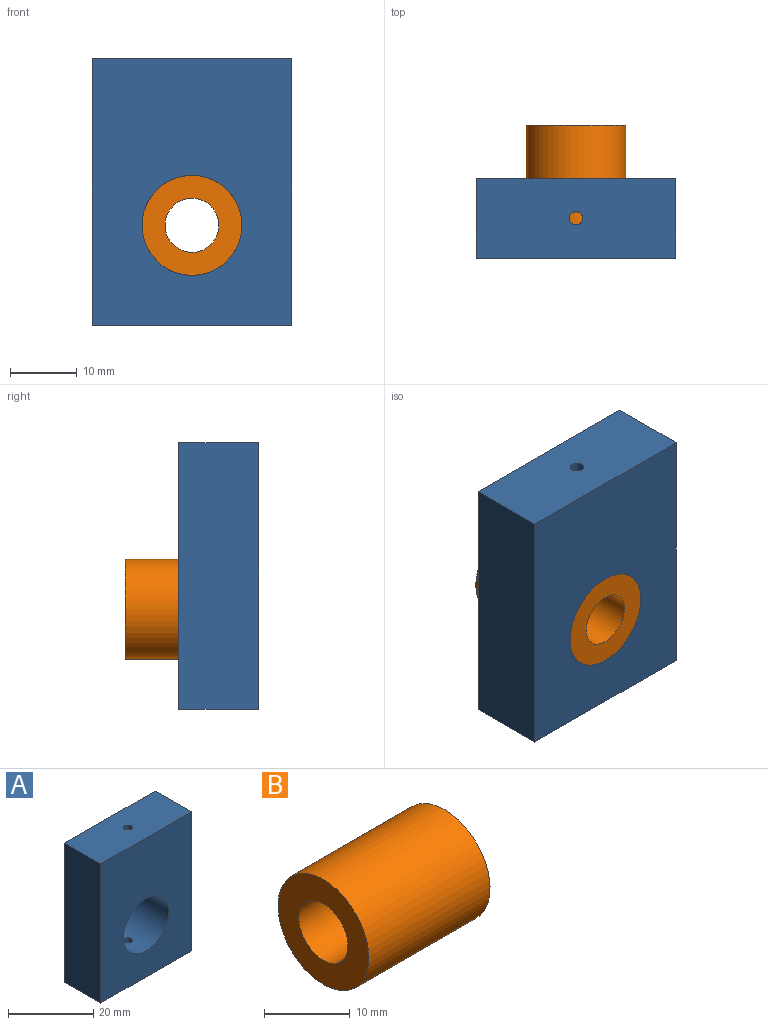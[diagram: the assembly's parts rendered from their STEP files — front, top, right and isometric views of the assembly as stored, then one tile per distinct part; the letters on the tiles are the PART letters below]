
ASSEMBLY  parts=2 mates=1
PART A: 9 faces, bbox 30x12x40 mm
  f0: plane 30x12mm, normal (0,0,1), area 356.9mm2, adj f1,f4,f5,f6,f8
  f1: plane 40x12mm, normal (-1,0,0), area 480mm2, adj f0,f2,f5,f6
  f2: plane 30x12mm, normal (0,0,-1), area 356.9mm2, adj f1,f4,f5,f6,f7
  f3: cylinder r=7.5mm len=15mm, axis (0,1,0), area 559.2mm2, adj f5,f6,f7,f8
  f4: plane 40x12mm, normal (1,0,0), area 480mm2, adj f0,f2,f5,f6
  f5: plane 40x30mm, normal (0,-1,0), area 1023.3mm2, adj f0,f1,f2,f3,f4
  f6: plane 40x30mm, normal (0,1,0), area 1023.3mm2, adj f0,f1,f2,f3,f4
  f7: cylinder r=1mm len=7.57mm, axis (0,0,1), area 47.3mm2, adj f2,f3
  f8: cylinder r=1mm len=17.57mm, axis (0,0,1), area 110.2mm2, adj f0,f3
PART B: 4 faces, bbox 20x15x15 mm
  f0: cylinder r=4.05mm len=20mm, axis (1,0,0), area 508.9mm2, adj f2,f3
  f1: cylinder r=7.5mm len=20mm, axis (1,0,0), area 942.5mm2, adj f2,f3
  f2: plane 15x15mm, normal (-1,0,0), area 125.2mm2, adj f0,f1
  f3: plane 15x15mm, normal (1,0,0), area 125.2mm2, adj f0,f1
PLACE A t=(-240.38,70.44,-349.7)mm
PLACE B rot(axis=(-0.58,0.58,-0.58),120deg) t=(-668.88,-11.56,372.8)mm
MATE fastened B.f0 <-> A.f3  axis (0,-1,0) through (-50.38,108.44,207.8)mm
